# Revit family: LB3S26337A75T-B,A2T-B
name_source: partatom
category: Plumbing Fixtures
units: mm (PartAtom-declared; Revit-internal decimal feet)

## family parameters
Always vertical = Yes
Cut with Voids When Loaded = No
OmniClass Number = 23.45.05.14.17
OmniClass Title = Showers
Part Type = Normal
Room Calculation Point = No
Round Connector Dimension = Use Diameter
Shared = No
Work Plane-Based = No

## types (4) — shared parameters
Assembly Code = D2010710
Keynote = 22 40 00.B3
Manufacturer = Best Bath Systems, Inc.
Type Comments = ADA Compliant
URL = http://www.bestbath.com
Unit Width = 63"

## per-type parameters (varying)
| type | Description | Threshold Height | Unit Height |
| LB3S26337A2B | "Subway Tile" 12" x 18", Beveled Threshold | 2" | 80" |
| LB3S26337A75B | "Subway Tile" 12" x 18", Beveled Threshold | 3/4" | 78 3/4" |
| LB3S26337A2T | "Subway Tile" 12" x 18", Traditional Bullnose Threshold | 2" | 80" |
| LB3S26337A75T | "Subway Tile" 12" x 18", Traditional Bullnose Threshold | 3/4" | 78 3/4" |

note: column(s) folded — value = type name in every type: Model

## geometry (parser evidence)
native form markers: Blend x12, Sweep x7
no freeform markers — native parametric forms only
